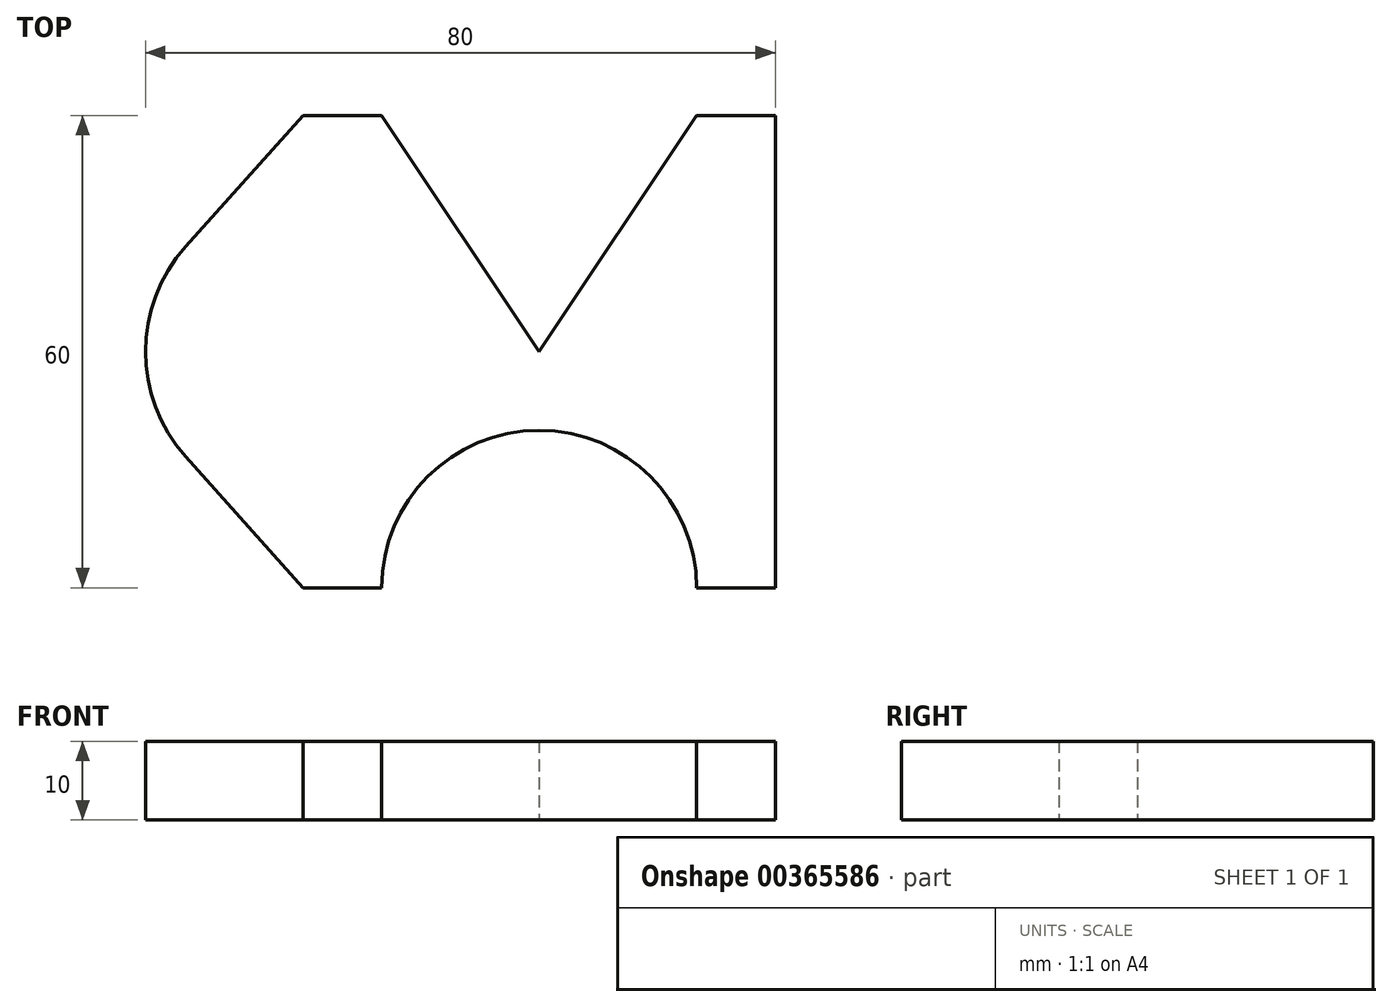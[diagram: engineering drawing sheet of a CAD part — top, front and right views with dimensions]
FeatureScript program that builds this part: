
annotation { "Feature Type Name" : "Feature", "Feature Type Description" : "" }
export const myFeature = defineFeature(function(context is Context, id is Id, definition is map)
    precondition{}
    {
        {
            var Q0;
            Q0=qCreatedBy(makeId("Top.planeOp"),FACE);
            var sketch = newSketch(context, id + "F0", { "sketchPlane" : qUnion([Q0])});
            skLineSegment(sketch, "E0", {"start": v(0, 0) * mm, "end": v(20, 30) * mm});
            skLineSegment(sketch, "E1", {"start": v(20, 30) * mm, "end": v(30, 30) * mm});
            skLineSegment(sketch, "E2", {"start": v(30, 30) * mm, "end": v(30, -30) * mm});
            skLineSegment(sketch, "E3", {"start": v(30, -30) * mm, "end": v(20, -30) * mm});
            skArc(sketch, "E4", {"start": v(20, -30) * mm, "mid": v(14.14, -15.86) * mm, "end": v(0, -10) * mm});
            skLineSegment(sketch, "E5.MirrorCS", {"start": v(-20, 30) * mm, "end": v(-30, 30) * mm});
            skArc(sketch, "E6.MirrorCS", {"start": v(-20, -30) * mm, "mid": v(-14.14, -15.86) * mm, "end": v(0, -10) * mm});
            skLineSegment(sketch, "E7.MirrorCS", {"start": v(0, 0) * mm, "end": v(-20, 30) * mm});
            skLineSegment(sketch, "E8.MirrorCS", {"start": v(-30, -30) * mm, "end": v(-20, -30) * mm});
            skLineSegment(sketch, "E9", {"start": v(-30, 30) * mm, "end": v(-44.9, 13.33) * mm});
            skArc(sketch, "E10", {"start": v(-44.9, 13.33) * mm, "mid": v(-50, 0) * mm, "end": v(-44.9, -13.33) * mm});
            skLineSegment(sketch, "E11", {"start": v(-44.9, -13.33) * mm, "end": v(-30, -30) * mm});
            skSolve(sketch);
        }
        {
            var Q0;
            Q0 = qSketchRegion(id + "F0", true);
            extrude(context, id + "F1", {"entities" : qUnion([Q0]), "depth" : 10 * mm});
        }
    });
